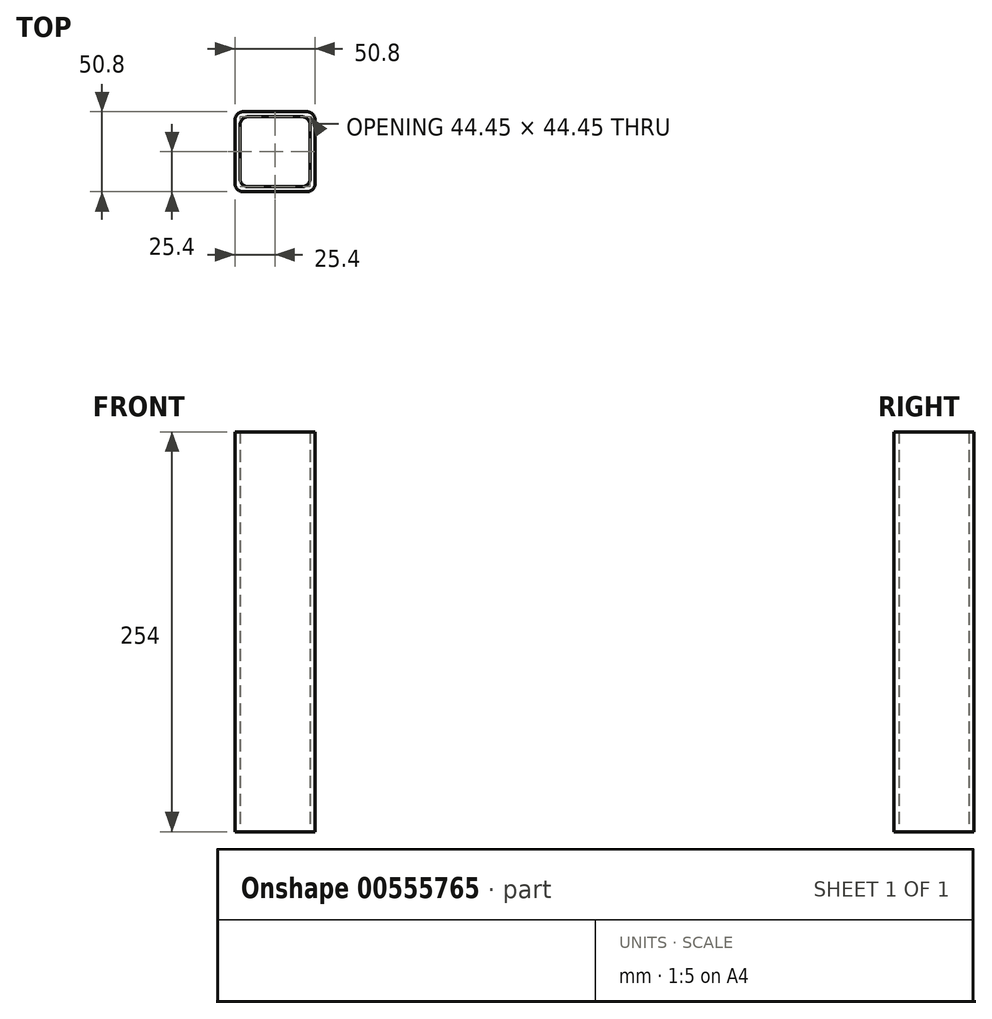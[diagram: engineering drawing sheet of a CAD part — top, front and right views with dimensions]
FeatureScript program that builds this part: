
annotation { "Feature Type Name" : "Feature", "Feature Type Description" : "" }
export const myFeature = defineFeature(function(context is Context, id is Id, definition is map)
    precondition{}
    {
        {
            var Q0;
            Q0=qCreatedBy(makeId("Top.planeOp"),FACE);
            var sketch = newSketch(context, id + "F0", { "sketchPlane" : qUnion([Q0])});
            skLineSegment(sketch, "E0.bottom", {"start": v(0, 0) * mm, "end": v(50.8, 0) * mm});
            skLineSegment(sketch, "E0.top", {"start": v(0, -50.8) * mm, "end": v(50.8, -50.8) * mm});
            skLineSegment(sketch, "E0.left", {"start": v(0, 0) * mm, "end": v(0, -50.8) * mm});
            skLineSegment(sketch, "E0.right", {"start": v(50.8, 0) * mm, "end": v(50.8, -50.8) * mm});
            skLineSegment(sketch, "E1.bottom", {"start": v(47.63, -47.63) * mm, "end": v(3.18, -47.63) * mm});
            skLineSegment(sketch, "E1.top", {"start": v(47.63, -3.18) * mm, "end": v(3.18, -3.18) * mm});
            skLineSegment(sketch, "E1.left", {"start": v(47.63, -47.62) * mm, "end": v(47.63, -3.18) * mm});
            skLineSegment(sketch, "E1.right", {"start": v(3.18, -47.63) * mm, "end": v(3.18, -3.18) * mm});
            skPoint(sketch, "E1.middle", {"position": v(25.4, -25.4) * mm});
            skSolve(sketch);
        }
        {
            var Q0;
            Q0=makeQuery(id+"F0.imprint","IMPRINT",FACE,{"disambiguationData":[TD([[makeQuery(id+"F0.imprint","IMPRINT",EDGE,{"derivedFrom":sQuery(id+"F0.wireOp",EDGE,"E0.bottom")}),-1.0]])]});
            extrude(context, id + "F1", {"entities" : qUnion([Q0]), "depth" : 254 * mm, "offsetDistance" : 25.4 * mm});
        }
        {
            var Q0;
            Q0=makeQuery(id+"F1.opExtrude","SWEPT_EDGE",EDGE,{"disambiguationData":[OSD([sQuery(id+"F0.wireOp",EDGE,"E0.top"),sQuery(id+"F0.wireOp",EDGE,"E0.right")])]});
            var Q1;
            Q1=makeQuery(id+"F1.opExtrude","SWEPT_EDGE",EDGE,{"disambiguationData":[OSD([sQuery(id+"F0.wireOp",EDGE,"E0.top"),sQuery(id+"F0.wireOp",EDGE,"E0.left")])]});
            var Q2;
            Q2=makeQuery(id+"F1.opExtrude","SWEPT_EDGE",EDGE,{"disambiguationData":[OSD([sQuery(id+"F0.wireOp",EDGE,"E0.bottom"),sQuery(id+"F0.wireOp",EDGE,"E0.right")])]});
            var Q3;
            Q3=makeQuery(id+"F1.opExtrude","SWEPT_EDGE",EDGE,{"disambiguationData":[OSD([sQuery(id+"F0.wireOp",EDGE,"E0.bottom"),sQuery(id+"F0.wireOp",EDGE,"E0.left")])]});
            var Q4;
            Q4=makeQuery(id+"F1.opExtrude","SWEPT_EDGE",EDGE,{"disambiguationData":[OSD([sQuery(id+"F0.wireOp",EDGE,"E1.top"),sQuery(id+"F0.wireOp",EDGE,"E1.left")])]});
            var Q5;
            Q5=makeQuery(id+"F1.opExtrude","SWEPT_EDGE",EDGE,{"disambiguationData":[OSD([sQuery(id+"F0.wireOp",EDGE,"E1.top"),sQuery(id+"F0.wireOp",EDGE,"E1.right")])]});
            var Q6;
            Q6=makeQuery(id+"F1.opExtrude","SWEPT_EDGE",EDGE,{"disambiguationData":[OSD([sQuery(id+"F0.wireOp",EDGE,"E1.bottom"),sQuery(id+"F0.wireOp",EDGE,"E1.right")])]});
            var Q7;
            Q7=makeQuery(id+"F1.opExtrude","SWEPT_EDGE",EDGE,{"disambiguationData":[OSD([sQuery(id+"F0.wireOp",EDGE,"E1.bottom"),sQuery(id+"F0.wireOp",EDGE,"E1.left")])]});
            fillet(context, id + "F2", {"entities" : qUnion([Q0, Q1, Q2, Q3, Q4, Q5, Q6, Q7]), "radius" : 5.08 * mm, "tangentPropagation" : true, "allowEdgeOverflow" : false});
        }
    });
